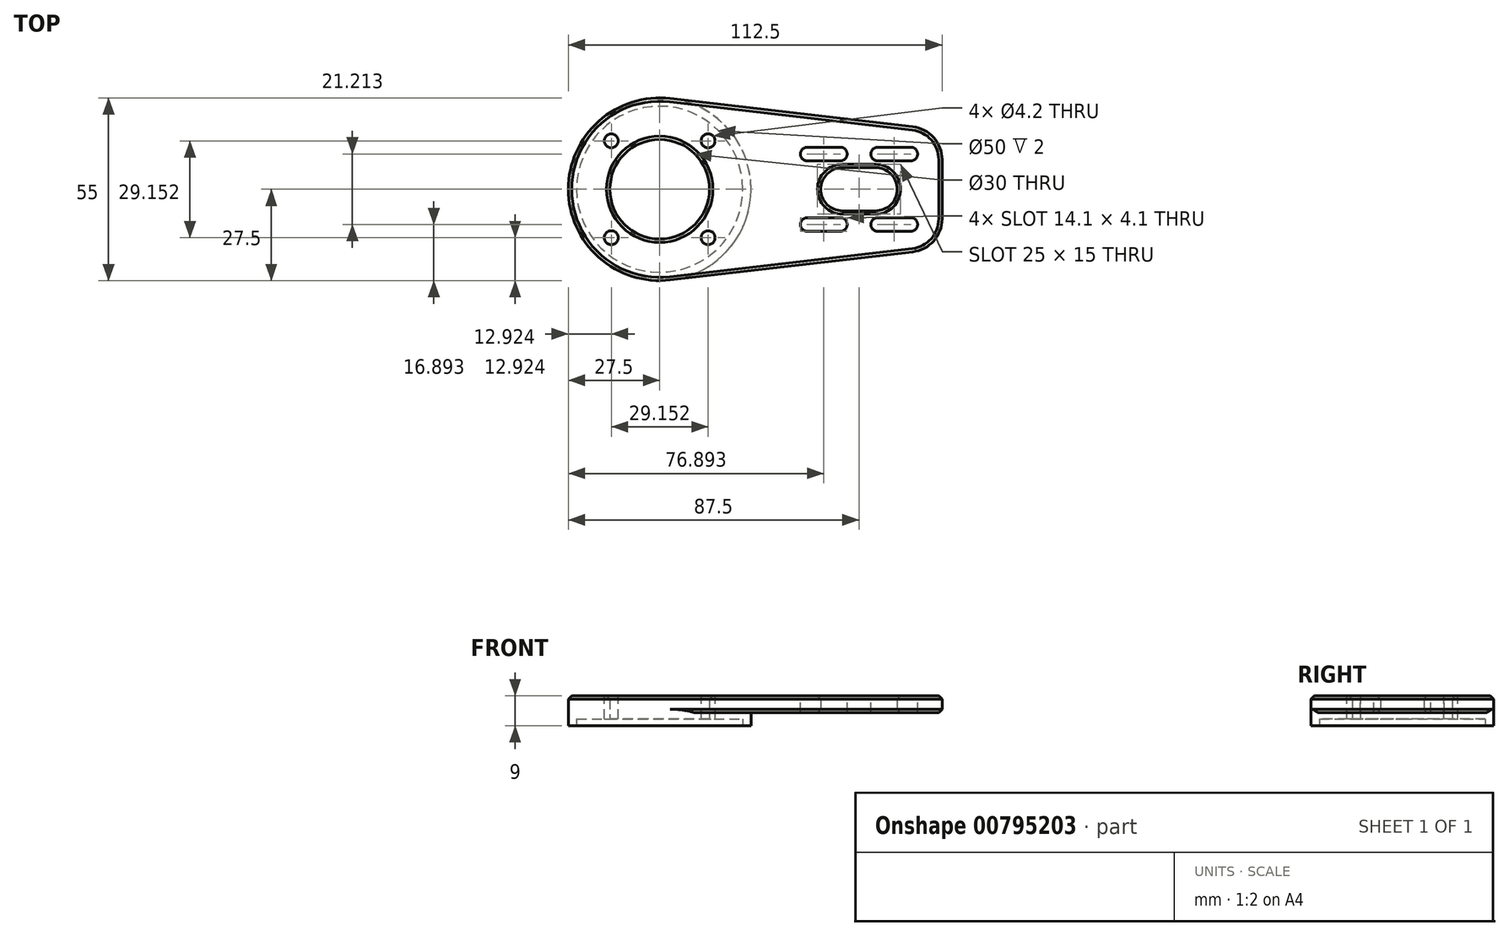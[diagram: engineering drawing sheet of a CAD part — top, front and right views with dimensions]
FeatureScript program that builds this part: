
annotation { "Feature Type Name" : "Feature", "Feature Type Description" : "" }
export const myFeature = defineFeature(function(context is Context, id is Id, definition is map)
    precondition{}
    {
        {
            var Q0;
            Q0=qCreatedBy(makeId("Top.planeOp"),FACE);
            var sketch = newSketch(context, id + "F0", { "sketchPlane" : qUnion([Q0])});
            skCircle(sketch, "E0", {"center": v(0, 0) * mm, "radius": 15 * mm});
            skArc(sketch, "E1", {"start": v(3.17, 27.32) * mm, "mid": v(1.59, 27.45) * mm, "end": v(0, 27.5) * mm});
            skLineSegment(sketch, "E2", {"start": v(3.17, 27.32) * mm, "end": v(76.15, 18.84) * mm});
            skLineSegment(sketch, "E3", {"start": v(76.15, -18.84) * mm, "end": v(3.17, -27.32) * mm});
            skArc(sketch, "E4", {"start": v(65, -6.5) * mm, "mid": v(71.5, 0) * mm, "end": v(65, 6.5) * mm});
            skArc(sketch, "E5", {"start": v(55, 6.5) * mm, "mid": v(48.5, 0) * mm, "end": v(55, -6.5) * mm});
            skLineSegment(sketch, "E6", {"start": v(55, 6.5) * mm, "end": v(65, 6.5) * mm});
            skLineSegment(sketch, "E7", {"start": v(65, -6.5) * mm, "end": v(55, -6.5) * mm});
            skLineSegment(sketch, "E8", {"start": v(85, -8.9) * mm, "end": v(85, 8.9) * mm});
            skPoint(sketch, "E9.orphan", {"position": v(85, 0) * mm});
            skArc(sketch, "E10.filletArc", {"start": v(85, 8.9) * mm, "mid": v(82.47, 15.56) * mm, "end": v(76.15, 18.84) * mm});
            skArc(sketch, "E11.filletArc", {"start": v(76.15, -18.84) * mm, "mid": v(82.47, -15.56) * mm, "end": v(85, -8.9) * mm});
            skPoint(sketch, "E12.visualSharp", {"position": v(-27.5, 27.5) * mm});
            skArc(sketch, "E13.trimOffspring", {"start": v(0, 27.5) * mm, "mid": v(-27.45, -1.59) * mm, "end": v(3.17, -27.32) * mm});
            skSolve(sketch);
        }
        {
            var Q0;
            Q0=makeQuery(id+"F0.imprint","IMPRINT",FACE,{"disambiguationData":[TD([[makeQuery(id+"F0.imprint","IMPRINT",EDGE,{"derivedFrom":sQuery(id+"F0.wireOp",EDGE,"E0")}),-1.0]])]});
            extrude(context, id + "F1", {"entities" : qUnion([Q0]), "depth" : 19 * mm, "offsetDistance" : 25 * mm});
        }
        {
            var Q0;
            Q0=makeQuery(id+"F1.opExtrude","CAP_FACE",FACE,{"disambiguationData":[OSD([sQuery(id+"F0.wireOp",EDGE,"E0"),sQuery(id+"F0.wireOp",EDGE,"E1"),sQuery(id+"F0.wireOp",EDGE,"N9EUgCCw-MTWe-O0Tq-X0WE-YSWXLGKSxSo5"),sQuery(id+"F0.wireOp",EDGE,"E2"),sQuery(id+"F0.wireOp",EDGE,"E3"),sQuery(id+"F0.wireOp",EDGE,"E4")])],"isStart":true});
            var sketch = newSketch(context, id + "F2", { "sketchPlane" : qUnion([Q0])});
            skLineSegment(sketch, "E14.0.0", {"start": v(76.15, 18.84) * mm, "end": v(3.17, 27.32) * mm});
            skLineSegment(sketch, "E14.0.2", {"start": v(3.17, -27.32) * mm, "end": v(3.17, -27.32) * mm});
            skArc(sketch, "E15", {"start": v(3.17, -27.32) * mm, "mid": v(27.5, 0) * mm, "end": v(3.17, 27.32) * mm});
            skLineSegment(sketch, "E16.bottom", {"start": v(3.17, 27.32) * mm, "end": v(88.11, 27.32) * mm});
            skLineSegment(sketch, "E16.top", {"start": v(3.17, -30.85) * mm, "end": v(88.11, -30.85) * mm});
            skLineSegment(sketch, "E16.left", {"start": v(3.17, -27.32) * mm, "end": v(3.17, -30.85) * mm});
            skLineSegment(sketch, "E16.right", {"start": v(88.11, 27.32) * mm, "end": v(88.11, -30.85) * mm});
            skSolve(sketch);
        }
        {
            var Q0;
            Q0=makeQuery(id+"F2.imprint","IMPRINT",FACE,{"disambiguationData":[TD([[makeQuery(id+"F2.imprint","IMPRINT",EDGE,{"derivedFrom":sQuery(id+"F2.wireOp",EDGE,"E15")}),-1.0]])]});
            extrude(context, id + "F3", {"entities" : qUnion([Q0]), "operationType" : NewBodyOperationType.REMOVE, "oppositeDirection" : true, "depth" : 10 * mm, "offsetDistance" : 25 * mm});
        }
        {
            var Q0;
            Q0=makeQuery(id+"F1.opExtrude","CAP_FACE",FACE,{"disambiguationData":[OSD([sQuery(id+"F0.wireOp",EDGE,"E0"),sQuery(id+"F0.wireOp",EDGE,"E1"),sQuery(id+"F0.wireOp",EDGE,"N9EUgCCw-MTWe-O0Tq-X0WE-YSWXLGKSxSo5"),sQuery(id+"F0.wireOp",EDGE,"E2"),sQuery(id+"F0.wireOp",EDGE,"E3"),sQuery(id+"F0.wireOp",EDGE,"E4")])],"isStart":true});
            var sketch = newSketch(context, id + "F4", { "sketchPlane" : qUnion([Q0])});
            skCircle(sketch, "E17", {"center": v(0, 0) * mm, "radius": 25 * mm});
            skSolve(sketch);
        }
        {
            var Q0;
            Q0=makeQuery(id+"F4.imprint","IMPRINT",FACE,{"disambiguationData":[TD([[makeQuery(id+"F4.imprint","IMPRINT",EDGE,{"derivedFrom":sQuery(id+"F4.wireOp",EDGE,"E17")}),1.0]])]});
            extrude(context, id + "F5", {"entities" : qUnion([Q0]), "operationType" : NewBodyOperationType.REMOVE, "oppositeDirection" : true, "depth" : 12 * mm, "offsetDistance" : 25 * mm});
        }
        {
            var Q0;
            Q0=makeQuery(id+"F3.boolean.opBoolean","COPY",EDGE,{"derivedFrom":makeQuery(id+"F3.opExtrude","CAP_EDGE",EDGE,{"disambiguationData":[OSD([sQuery(id+"F2.wireOp",EDGE,"E15")])],"isStart":false})});
            fillet(context, id + "F6", {"entities" : qUnion([Q0]), "radius" : 2.5 * mm, "tangentPropagation" : true, "allowEdgeOverflow" : false});
        }
        {
            var Q0;
            Q0=makeQuery(id+"F1.opExtrude","CAP_EDGE",EDGE,{"disambiguationData":[OSD([sQuery(id+"F0.wireOp",EDGE,"E3")])],"isStart":false});
            var Q1;
            Q1=makeQuery(id+"F3.boolean.opBoolean","MERGE",EDGE,{"derivedFrom":[makeQuery(id+"F1.opExtrude","CAP_EDGE",EDGE,{"disambiguationData":[OSD([sQuery(id+"F0.wireOp",EDGE,"E1")])],"isStart":true}),makeQuery(id+"F3.opExtrude","CAP_EDGE",EDGE,{"disambiguationData":[OSD([sQuery(id+"F2.wireOp",EDGE,"E15")])],"isStart":true})]});
            chamfer(context, id + "F7", {"entities" : qUnion([Q0, Q1]), "width" : 1 * mm, "tangentPropagation" : true});
        }
        {
            var Q0;
            Q0=makeQuery(id+"F1.opExtrude","CAP_FACE",FACE,{"disambiguationData":[OSD([sQuery(id+"F0.wireOp",EDGE,"E0"),sQuery(id+"F0.wireOp",EDGE,"E1"),sQuery(id+"F0.wireOp",EDGE,"N9EUgCCw-MTWe-O0Tq-X0WE-YSWXLGKSxSo5"),sQuery(id+"F0.wireOp",EDGE,"E2"),sQuery(id+"F0.wireOp",EDGE,"E3"),sQuery(id+"F0.wireOp",EDGE,"E4")])],"isStart":false});
            var sketch = newSketch(context, id + "F8", { "sketchPlane" : qUnion([Q0])});
            skCircle(sketch, "E18", {"center": v(65, 0) * mm, "radius": 15 * mm, "construction": true});
            skLineSegment(sketch, "E19", {"start": v(65, 0) * mm, "end": v(65, 34.86) * mm, "construction": true});
            skLineSegment(sketch, "E20", {"start": v(65, 0) * mm, "end": v(50.97, 14.03) * mm, "construction": true});
            skLineSegment(sketch, "E21", {"start": v(54.4, 10.6) * mm, "end": v(44.4, 10.6) * mm, "construction": true});
            skLineSegment(sketch, "E22", {"start": v(75.6, 10.6) * mm, "end": v(65.6, 10.6) * mm, "construction": true});
            skLineSegment(sketch, "E23", {"start": v(75.6, -10.6) * mm, "end": v(65.6, -10.6) * mm, "construction": true});
            skLineSegment(sketch, "E24", {"start": v(54.4, -10.6) * mm, "end": v(44.4, -10.6) * mm, "construction": true});
            skArc(sketch, "E25.0.startCap", {"start": v(54.4, 12.66) * mm, "mid": v(56.44, 10.6) * mm, "end": v(54.4, 8.56) * mm});
            skArc(sketch, "E25.0.endCap", {"start": v(44.4, 8.56) * mm, "mid": v(42.34, 10.6) * mm, "end": v(44.4, 12.66) * mm});
            skLineSegment(sketch, "E25.0.left", {"start": v(54.4, 8.56) * mm, "end": v(44.4, 8.56) * mm});
            skLineSegment(sketch, "E25.0.right", {"start": v(54.4, 12.66) * mm, "end": v(44.4, 12.66) * mm});
            skArc(sketch, "E26.0.startCap", {"start": v(75.6, 12.66) * mm, "mid": v(77.66, 10.6) * mm, "end": v(75.6, 8.56) * mm});
            skArc(sketch, "E26.0.endCap", {"start": v(65.6, 8.56) * mm, "mid": v(63.56, 10.6) * mm, "end": v(65.6, 12.66) * mm});
            skLineSegment(sketch, "E26.0.left", {"start": v(75.6, 8.56) * mm, "end": v(65.6, 8.56) * mm});
            skLineSegment(sketch, "E26.0.right", {"start": v(75.6, 12.66) * mm, "end": v(65.6, 12.66) * mm});
            skArc(sketch, "E26.1.startCap", {"start": v(75.6, -8.56) * mm, "mid": v(77.66, -10.6) * mm, "end": v(75.6, -12.66) * mm});
            skArc(sketch, "E26.1.endCap", {"start": v(65.6, -12.66) * mm, "mid": v(63.56, -10.6) * mm, "end": v(65.6, -8.56) * mm});
            skLineSegment(sketch, "E26.1.left", {"start": v(75.6, -12.66) * mm, "end": v(65.6, -12.66) * mm});
            skLineSegment(sketch, "E26.1.right", {"start": v(75.6, -8.56) * mm, "end": v(65.6, -8.56) * mm});
            skArc(sketch, "E26.2.startCap", {"start": v(54.4, -8.56) * mm, "mid": v(56.44, -10.6) * mm, "end": v(54.4, -12.66) * mm});
            skArc(sketch, "E26.2.endCap", {"start": v(44.4, -12.66) * mm, "mid": v(42.34, -10.6) * mm, "end": v(44.4, -8.56) * mm});
            skLineSegment(sketch, "E26.2.left", {"start": v(54.4, -12.66) * mm, "end": v(44.4, -12.66) * mm});
            skLineSegment(sketch, "E26.2.right", {"start": v(54.4, -8.56) * mm, "end": v(44.4, -8.56) * mm});
            skSolve(sketch);
        }
        {
            var Q0;
            Q0 = qSketchRegion(id + "F8", true);
            extrude(context, id + "F9", {"entities" : qUnion([Q0]), "operationType" : NewBodyOperationType.REMOVE, "oppositeDirection" : true, "depth" : 25 * mm, "offsetDistance" : 25 * mm});
        }
        {
            var Q0;
            Q0=makeQuery(id+"F1.opExtrude","CAP_FACE",FACE,{"disambiguationData":[OSD([sQuery(id+"F0.wireOp",EDGE,"E0"),sQuery(id+"F0.wireOp",EDGE,"E1"),sQuery(id+"F0.wireOp",EDGE,"E2"),sQuery(id+"F0.wireOp",EDGE,"E3"),sQuery(id+"F0.wireOp",EDGE,"E4"),sQuery(id+"F0.wireOp",EDGE,"E5"),sQuery(id+"F0.wireOp",EDGE,"E6"),sQuery(id+"F0.wireOp",EDGE,"E7"),sQuery(id+"F0.wireOp",EDGE,"E8"),sQuery(id+"F0.wireOp",EDGE,"E10.filletArc"),sQuery(id+"F0.wireOp",EDGE,"E11.filletArc"),sQuery(id+"F0.wireOp",EDGE,"E13.trimOffspring")])],"isStart":true});
            var sketch = newSketch(context, id + "F10", { "sketchPlane" : qUnion([Q0])});
            skCircle(sketch, "E27", {"center": v(0, 0) * mm, "radius": 98.81 * mm});
            skSolve(sketch);
        }
        {
            var Q0;
            Q0 = qSketchRegion(id + "F10", true);
            var Q1;
            Q1=makeQuery(id+"F3.boolean.opBoolean","COPY",FACE,{"derivedFrom":makeQuery(id+"F3.opExtrude","CAP_FACE",FACE,{"disambiguationData":[OSD([sQuery(id+"F0.wireOp",EDGE,"E2"),sQuery(id+"F0.wireOp",EDGE,"E4"),sQuery(id+"F0.wireOp",EDGE,"E5"),sQuery(id+"F0.wireOp",EDGE,"E6"),sQuery(id+"F0.wireOp",EDGE,"E7"),sQuery(id+"F0.wireOp",EDGE,"E8"),sQuery(id+"F0.wireOp",EDGE,"E10.filletArc"),sQuery(id+"F0.wireOp",EDGE,"E11.filletArc"),sQuery(id+"F2.wireOp",EDGE,"E14.0.0"),sQuery(id+"F2.wireOp",EDGE,"E15")])],"isStart":false})});
            extrude(context, id + "F11", {"entities" : qUnion([Q0]), "operationType" : NewBodyOperationType.REMOVE, "endBound" : BoundingType.UP_TO_SURFACE, "oppositeDirection" : true, "depth" : 25 * mm, "endBoundEntityFace" : qUnion([Q1]), "offsetDistance" : 25 * mm});
        }
        {
            var Q0;
            Q0=makeQuery(id+"F1.opExtrude","CAP_FACE",FACE,{"disambiguationData":[OSD([sQuery(id+"F0.wireOp",EDGE,"E0"),sQuery(id+"F0.wireOp",EDGE,"E1"),sQuery(id+"F0.wireOp",EDGE,"E2"),sQuery(id+"F0.wireOp",EDGE,"E3"),sQuery(id+"F0.wireOp",EDGE,"E4"),sQuery(id+"F0.wireOp",EDGE,"E5"),sQuery(id+"F0.wireOp",EDGE,"E6"),sQuery(id+"F0.wireOp",EDGE,"E7"),sQuery(id+"F0.wireOp",EDGE,"E8"),sQuery(id+"F0.wireOp",EDGE,"E10.filletArc"),sQuery(id+"F0.wireOp",EDGE,"E11.filletArc"),sQuery(id+"F0.wireOp",EDGE,"E13.trimOffspring")])],"isStart":false});
            var sketch = newSketch(context, id + "F12", { "sketchPlane" : qUnion([Q0])});
            skCircle(sketch, "E28", {"center": v(0, 0) * mm, "radius": 20.5 * mm, "construction": true});
            skLineSegment(sketch, "E29", {"start": v(0, 0) * mm, "end": v(-24.16, 24.16) * mm, "construction": true});
            skCircle(sketch, "E30", {"center": v(-14.58, 14.58) * mm, "radius": 2.1 * mm});
            skCircle(sketch, "E31.1.0", {"center": v(-14.58, -14.58) * mm, "radius": 2.1 * mm});
            skCircle(sketch, "E31.2.0", {"center": v(14.58, -14.58) * mm, "radius": 2.1 * mm});
            skCircle(sketch, "E31.3.0", {"center": v(14.58, 14.58) * mm, "radius": 2.1 * mm});
            skSolve(sketch);
        }
        {
            var Q0;
            Q0 = qSketchRegion(id + "F12", true);
            extrude(context, id + "F13", {"entities" : qUnion([Q0]), "operationType" : NewBodyOperationType.REMOVE, "endBound" : BoundingType.THROUGH_ALL, "oppositeDirection" : true, "depth" : 25 * mm, "offsetDistance" : 25 * mm});
        }
        {
            var Q0;
            {var subQ0=sQuery(id+"F2.wireOp",EDGE,"E15");var subQ1=sQuery(id+"F2.wireOp",EDGE,"E14.0.0");var subQ2=sQuery(id+"F0.wireOp",EDGE,"E11.filletArc");var subQ3=sQuery(id+"F0.wireOp",EDGE,"E10.filletArc");var subQ4=sQuery(id+"F0.wireOp",EDGE,"E8");var subQ5=sQuery(id+"F0.wireOp",EDGE,"E7");var subQ6=sQuery(id+"F0.wireOp",EDGE,"E6");var subQ7=sQuery(id+"F0.wireOp",EDGE,"E5");var subQ8=sQuery(id+"F0.wireOp",EDGE,"E4");var subQ9=sQuery(id+"F0.wireOp",EDGE,"E2");Q0=makeQuery(id+"F11.boolean.opBoolean","MERGE",FACE,{"derivedFrom":[makeQuery(id+"F3.boolean.opBoolean","COPY",FACE,{"derivedFrom":makeQuery(id+"F3.opExtrude","CAP_FACE",FACE,{"disambiguationData":[OSD([subQ9,subQ8,subQ7,subQ6,subQ5,subQ4,subQ3,subQ2,subQ1,subQ0])],"isStart":false})}),makeQuery(id+"F11.opExtrude","CAP_FACE",FACE,{"disambiguationData":[OSD([subQ9,subQ8,subQ7,subQ6,subQ5,subQ4,subQ3,subQ2,subQ1,subQ0])],"isStart":false})]});}
            var sketch = newSketch(context, id + "F14", { "sketchPlane" : qUnion([Q0])});
            skArc(sketch, "E32", {"start": v(0, -27.5) * mm, "mid": v(27.5, 0) * mm, "end": v(0, 27.5) * mm});
            skLineSegment(sketch, "E33.bottom", {"start": v(0, -27.5) * mm, "end": v(90.4, -27.5) * mm});
            skLineSegment(sketch, "E33.top", {"start": v(0, 28.36) * mm, "end": v(90.4, 28.36) * mm});
            skLineSegment(sketch, "E33.right", {"start": v(90.4, -27.5) * mm, "end": v(90.4, 28.36) * mm});
            skLineSegment(sketch, "E34.trimOffspring", {"start": v(0, 27.5) * mm, "end": v(0, 28.36) * mm});
            skSolve(sketch);
        }
        {
            var Q0;
            Q0 = qSketchRegion(id + "F14", true);
            extrude(context, id + "F15", {"entities" : qUnion([Q0]), "operationType" : NewBodyOperationType.REMOVE, "oppositeDirection" : true, "depth" : 4 * mm, "offsetDistance" : 25 * mm});
        }
        {
            var Q0;
            Q0=makeQuery(id+"F15.boolean.opBoolean","INTERSECT",EDGE,{"derivedFrom":[makeQuery(id+"F1.opExtrude","SWEPT_FACE",FACE,{"disambiguationData":[OSD([sQuery(id+"F0.wireOp",EDGE,"E3")])]}),makeQuery(id+"F15.opExtrude","CAP_FACE",FACE,{"disambiguationData":[OSD([sQuery(id+"F14.wireOp",EDGE,"E32"),sQuery(id+"F14.wireOp",EDGE,"E33.bottom"),sQuery(id+"F14.wireOp",EDGE,"E33.top"),sQuery(id+"F14.wireOp",EDGE,"E33.right"),sQuery(id+"F14.wireOp",EDGE,"E34.trimOffspring")])],"isStart":false})]});
            var Q1;
            {var subQ0=sQuery(id+"F2.wireOp",EDGE,"E15");Q1=makeQuery(id+"F15.boolean.opBoolean","MERGE",EDGE,{"derivedFrom":[makeQuery(id+"F11.boolean.opBoolean","INTERSECT",EDGE,{"derivedFrom":[makeQuery(id+"F3.boolean.opBoolean","MERGE",FACE,{"derivedFrom":[makeQuery(id+"F1.opExtrude","SWEPT_FACE",FACE,{"disambiguationData":[OSD([sQuery(id+"F0.wireOp",EDGE,"E1"),sQuery(id+"F0.wireOp",EDGE,"E13.trimOffspring")])]}),makeQuery(id+"F3.opExtrude","SWEPT_FACE",FACE,{"disambiguationData":[OSD([subQ0])]})]}),makeQuery(id+"F11.opExtrude","CAP_FACE",FACE,{"disambiguationData":[OSD([sQuery(id+"F0.wireOp",EDGE,"E2"),sQuery(id+"F0.wireOp",EDGE,"E4"),sQuery(id+"F0.wireOp",EDGE,"E5"),sQuery(id+"F0.wireOp",EDGE,"E6"),sQuery(id+"F0.wireOp",EDGE,"E7"),sQuery(id+"F0.wireOp",EDGE,"E8"),sQuery(id+"F0.wireOp",EDGE,"E10.filletArc"),sQuery(id+"F0.wireOp",EDGE,"E11.filletArc"),sQuery(id+"F2.wireOp",EDGE,"E14.0.0"),subQ0])],"isStart":false})]}),makeQuery(id+"F15.opExtrude","CAP_EDGE",EDGE,{"disambiguationData":[OSD([sQuery(id+"F14.wireOp",EDGE,"E32")])],"isStart":true})]});}
            chamfer(context, id + "F16", {"entities" : qUnion([Q0, Q1]), "width" : 1 * mm, "tangentPropagation" : true});
        }
        {
            var Q0;
            Q0=makeQuery(id+"F1.opExtrude","CAP_EDGE",EDGE,{"disambiguationData":[OSD([sQuery(id+"F0.wireOp",EDGE,"E0")])],"isStart":false});
            var Q1;
            Q1=makeQuery(id+"F1.opExtrude","CAP_EDGE",EDGE,{"disambiguationData":[OSD([sQuery(id+"F0.wireOp",EDGE,"E6")])],"isStart":false});
            var Q2;
            Q2=makeQuery(id+"F15.boolean.opBoolean","INTERSECT",EDGE,{"derivedFrom":[makeQuery(id+"F1.opExtrude","SWEPT_FACE",FACE,{"disambiguationData":[OSD([sQuery(id+"F0.wireOp",EDGE,"E4")])]}),makeQuery(id+"F15.opExtrude","CAP_FACE",FACE,{"disambiguationData":[OSD([sQuery(id+"F14.wireOp",EDGE,"E32"),sQuery(id+"F14.wireOp",EDGE,"E33.bottom"),sQuery(id+"F14.wireOp",EDGE,"E33.top"),sQuery(id+"F14.wireOp",EDGE,"E33.right"),sQuery(id+"F14.wireOp",EDGE,"E34.trimOffspring")])],"isStart":false})]});
            chamfer(context, id + "F17", {"entities" : qUnion([Q0, Q1, Q2]), "width" : 1 * mm, "tangentPropagation" : true});
        }
    });
